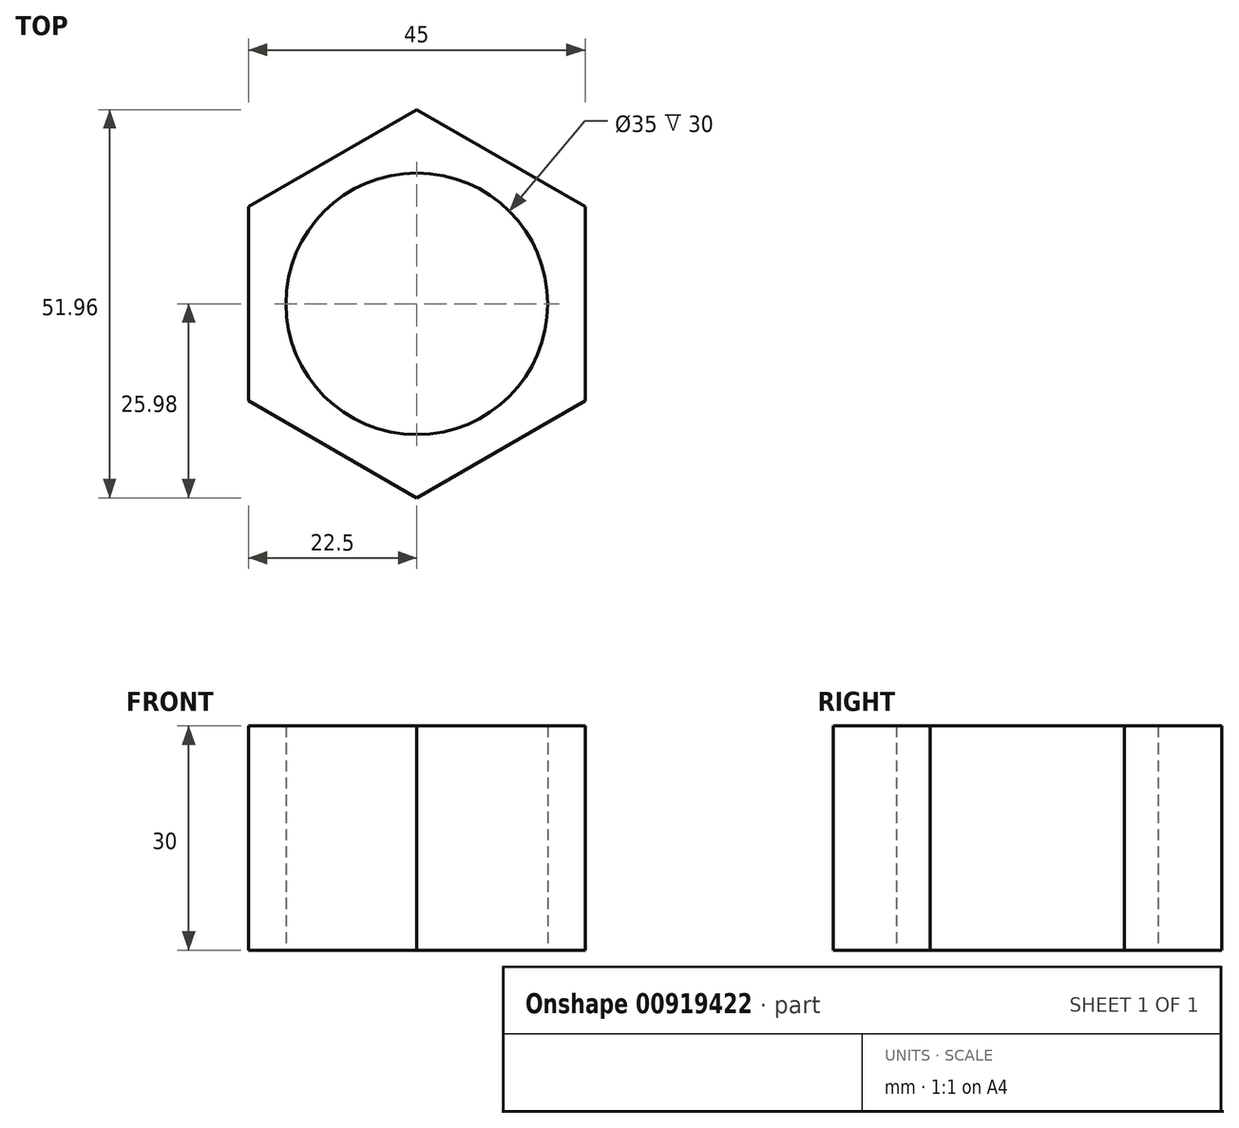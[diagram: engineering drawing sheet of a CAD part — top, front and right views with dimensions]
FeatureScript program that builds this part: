
annotation { "Feature Type Name" : "Feature", "Feature Type Description" : "" }
export const myFeature = defineFeature(function(context is Context, id is Id, definition is map)
    precondition{}
    {
        {
            var Q0;
            Q0=qCreatedBy(makeId("Top.planeOp"),FACE);
            var sketch = newSketch(context, id + "F0", { "sketchPlane" : qUnion([Q0])});
            skCircle(sketch, "E0.cCircle", {"center": v(0, 0) * mm, "radius": 22.5 * mm, "construction": true});
            skLineSegment(sketch, "E0.0", {"start": v(-22.5, -13) * mm, "end": v(-22.5, 13) * mm});
            skLineSegment(sketch, "E0.1", {"start": v(-22.5, 13) * mm, "end": v(0, 25.98) * mm});
            skLineSegment(sketch, "E0.2", {"start": v(0, 25.98) * mm, "end": v(22.5, 13) * mm});
            skLineSegment(sketch, "E0.3", {"start": v(22.5, 13) * mm, "end": v(22.5, -13) * mm});
            skLineSegment(sketch, "E0.4", {"start": v(22.5, -13) * mm, "end": v(0, -25.98) * mm});
            skLineSegment(sketch, "E0.5", {"start": v(0, -25.98) * mm, "end": v(-22.5, -13) * mm});
            skPoint(sketch, "E0.0.midPoint", {"position": v(-22.5, 0) * mm});
            skCircle(sketch, "E1", {"center": v(0, 0) * mm, "radius": 17.5 * mm});
            skSolve(sketch);
        }
        {
            var Q0;
            Q0=makeQuery(id+"F0.imprint","IMPRINT",FACE,{"disambiguationData":[TD([[makeQuery(id+"F0.imprint","IMPRINT",EDGE,{"derivedFrom":sQuery(id+"F0.wireOp",EDGE,"E0.0")}),-1.0]])]});
            extrude(context, id + "F1", {"entities" : qUnion([Q0]), "endBound" : BoundingType.SYMMETRIC, "depth" : 30 * mm, "offsetDistance" : 25 * mm});
        }
    });
